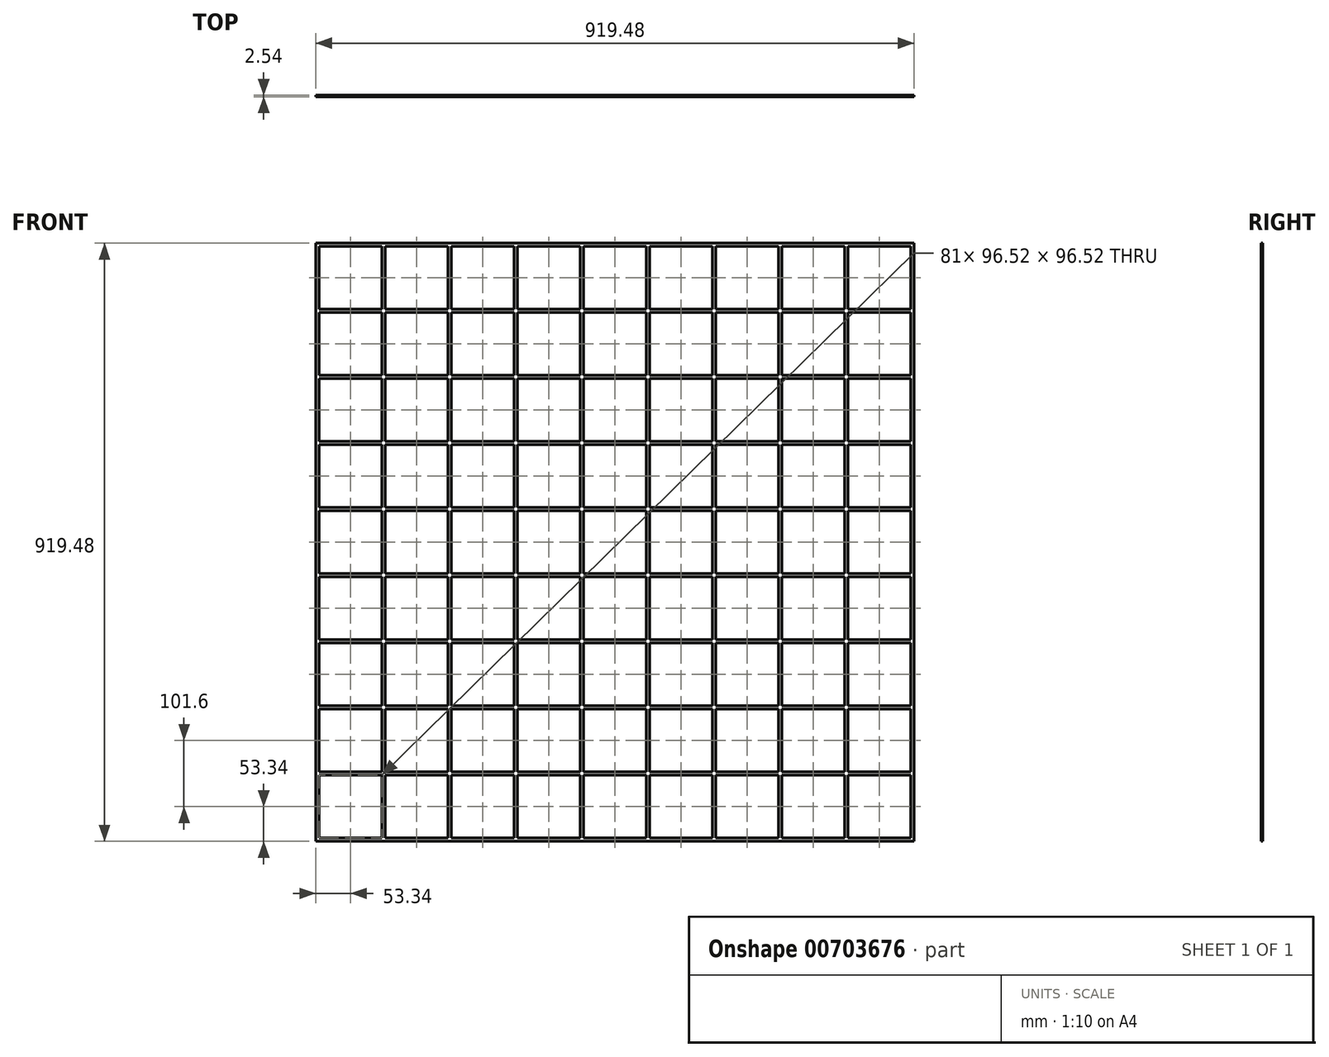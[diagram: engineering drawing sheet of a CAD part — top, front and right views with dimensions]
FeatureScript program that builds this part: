
annotation { "Feature Type Name" : "Feature", "Feature Type Description" : "" }
export const myFeature = defineFeature(function(context is Context, id is Id, definition is map)
    precondition{}
    {
        {
            var Q0;
            Q0=qCreatedBy(makeId("Front.planeOp"),FACE);
            var sketch = newSketch(context, id + "F0", { "sketchPlane" : qUnion([Q0])});
            skLineSegment(sketch, "E0.bottom", {"start": v(0, 0) * mm, "end": v(919.48, 0) * mm});
            skLineSegment(sketch, "E0.top", {"start": v(0, 919.48) * mm, "end": v(919.48, 919.48) * mm});
            skLineSegment(sketch, "E0.left", {"start": v(0, 0) * mm, "end": v(0, 919.48) * mm});
            skLineSegment(sketch, "E0.right", {"start": v(919.48, 0) * mm, "end": v(919.48, 919.48) * mm});
            skSolve(sketch);
        }
        {
            var Q0;
            Q0 = qSketchRegion(id + "F0", true);
            extrude(context, id + "F1", {"entities" : qUnion([Q0]), "depth" : 2.54 * mm, "offsetDistance" : 25.4 * mm});
        }
        {
            var Q0;
            Q0=makeQuery(id+"F0.imprint","IMPRINT",FACE,{"disambiguationData":[TD([[makeQuery(id+"F0.imprint","IMPRINT",EDGE,{"derivedFrom":sQuery(id+"F0.wireOp",EDGE,"E0.bottom")}),1.0]])]});
            var sketch = newSketch(context, id + "F2", { "sketchPlane" : qUnion([Q0])});
            skLineSegment(sketch, "E1.bottom", {"start": v(5.08, 914.4) * mm, "end": v(101.6, 914.4) * mm});
            skLineSegment(sketch, "E1.top", {"start": v(5.08, 817.88) * mm, "end": v(101.6, 817.88) * mm});
            skLineSegment(sketch, "E1.left", {"start": v(5.08, 914.4) * mm, "end": v(5.08, 817.88) * mm});
            skLineSegment(sketch, "E1.right", {"start": v(101.6, 914.4) * mm, "end": v(101.6, 817.88) * mm});
            skLineSegment(sketch, "E2.0.1.0", {"start": v(101.6, 812.8) * mm, "end": v(101.6, 716.28) * mm});
            skLineSegment(sketch, "E2.0.1.1", {"start": v(5.08, 812.8) * mm, "end": v(101.6, 812.8) * mm});
            skLineSegment(sketch, "E2.0.1.2", {"start": v(5.08, 812.8) * mm, "end": v(5.08, 716.28) * mm});
            skLineSegment(sketch, "E2.0.1.3", {"start": v(5.08, 716.28) * mm, "end": v(101.6, 716.28) * mm});
            skLineSegment(sketch, "E2.0.2.0", {"start": v(101.6, 711.2) * mm, "end": v(101.6, 614.68) * mm});
            skLineSegment(sketch, "E2.0.2.1", {"start": v(5.08, 711.2) * mm, "end": v(101.6, 711.2) * mm});
            skLineSegment(sketch, "E2.0.2.2", {"start": v(5.08, 711.2) * mm, "end": v(5.08, 614.68) * mm});
            skLineSegment(sketch, "E2.0.2.3", {"start": v(5.08, 614.68) * mm, "end": v(101.6, 614.68) * mm});
            skLineSegment(sketch, "E2.0.3.0", {"start": v(101.6, 609.6) * mm, "end": v(101.6, 513.08) * mm});
            skLineSegment(sketch, "E2.0.3.1", {"start": v(5.08, 609.6) * mm, "end": v(101.6, 609.6) * mm});
            skLineSegment(sketch, "E2.0.3.2", {"start": v(5.08, 609.6) * mm, "end": v(5.08, 513.08) * mm});
            skLineSegment(sketch, "E2.0.3.3", {"start": v(5.08, 513.08) * mm, "end": v(101.6, 513.08) * mm});
            skLineSegment(sketch, "E2.0.4.0", {"start": v(101.6, 508) * mm, "end": v(101.6, 411.48) * mm});
            skLineSegment(sketch, "E2.0.4.1", {"start": v(5.08, 508) * mm, "end": v(101.6, 508) * mm});
            skLineSegment(sketch, "E2.0.4.2", {"start": v(5.08, 508) * mm, "end": v(5.08, 411.48) * mm});
            skLineSegment(sketch, "E2.0.4.3", {"start": v(5.08, 411.48) * mm, "end": v(101.6, 411.48) * mm});
            skLineSegment(sketch, "E2.0.5.0", {"start": v(101.6, 406.4) * mm, "end": v(101.6, 309.88) * mm});
            skLineSegment(sketch, "E2.0.5.1", {"start": v(5.08, 406.4) * mm, "end": v(101.6, 406.4) * mm});
            skLineSegment(sketch, "E2.0.5.2", {"start": v(5.08, 406.4) * mm, "end": v(5.08, 309.88) * mm});
            skLineSegment(sketch, "E2.0.5.3", {"start": v(5.08, 309.88) * mm, "end": v(101.6, 309.88) * mm});
            skLineSegment(sketch, "E2.0.6.0", {"start": v(101.6, 304.8) * mm, "end": v(101.6, 208.28) * mm});
            skLineSegment(sketch, "E2.0.6.1", {"start": v(5.08, 304.8) * mm, "end": v(101.6, 304.8) * mm});
            skLineSegment(sketch, "E2.0.6.2", {"start": v(5.08, 304.8) * mm, "end": v(5.08, 208.28) * mm});
            skLineSegment(sketch, "E2.0.6.3", {"start": v(5.08, 208.28) * mm, "end": v(101.6, 208.28) * mm});
            skLineSegment(sketch, "E2.0.7.0", {"start": v(101.6, 203.2) * mm, "end": v(101.6, 106.68) * mm});
            skLineSegment(sketch, "E2.0.7.1", {"start": v(5.08, 203.2) * mm, "end": v(101.6, 203.2) * mm});
            skLineSegment(sketch, "E2.0.7.2", {"start": v(5.08, 203.2) * mm, "end": v(5.08, 106.68) * mm});
            skLineSegment(sketch, "E2.0.7.3", {"start": v(5.08, 106.68) * mm, "end": v(101.6, 106.68) * mm});
            skLineSegment(sketch, "E2.0.8.0", {"start": v(101.6, 101.6) * mm, "end": v(101.6, 5.08) * mm});
            skLineSegment(sketch, "E2.0.8.1", {"start": v(5.08, 101.6) * mm, "end": v(101.6, 101.6) * mm});
            skLineSegment(sketch, "E2.0.8.2", {"start": v(5.08, 101.6) * mm, "end": v(5.08, 5.08) * mm});
            skLineSegment(sketch, "E2.0.8.3", {"start": v(5.08, 5.08) * mm, "end": v(101.6, 5.08) * mm});
            skLineSegment(sketch, "E2.1.0.0", {"start": v(203.2, 914.4) * mm, "end": v(203.2, 817.88) * mm});
            skLineSegment(sketch, "E2.1.0.1", {"start": v(106.68, 914.4) * mm, "end": v(203.2, 914.4) * mm});
            skLineSegment(sketch, "E2.1.0.2", {"start": v(106.68, 914.4) * mm, "end": v(106.68, 817.88) * mm});
            skLineSegment(sketch, "E2.1.0.3", {"start": v(106.68, 817.88) * mm, "end": v(203.2, 817.88) * mm});
            skLineSegment(sketch, "E2.1.1.0", {"start": v(203.2, 812.8) * mm, "end": v(203.2, 716.28) * mm});
            skLineSegment(sketch, "E2.1.1.1", {"start": v(106.68, 812.8) * mm, "end": v(203.2, 812.8) * mm});
            skLineSegment(sketch, "E2.1.1.2", {"start": v(106.68, 812.8) * mm, "end": v(106.68, 716.28) * mm});
            skLineSegment(sketch, "E2.1.1.3", {"start": v(106.68, 716.28) * mm, "end": v(203.2, 716.28) * mm});
            skLineSegment(sketch, "E2.1.2.0", {"start": v(203.2, 711.2) * mm, "end": v(203.2, 614.68) * mm});
            skLineSegment(sketch, "E2.1.2.1", {"start": v(106.68, 711.2) * mm, "end": v(203.2, 711.2) * mm});
            skLineSegment(sketch, "E2.1.2.2", {"start": v(106.68, 711.2) * mm, "end": v(106.68, 614.68) * mm});
            skLineSegment(sketch, "E2.1.2.3", {"start": v(106.68, 614.68) * mm, "end": v(203.2, 614.68) * mm});
            skLineSegment(sketch, "E2.1.3.0", {"start": v(203.2, 609.6) * mm, "end": v(203.2, 513.08) * mm});
            skLineSegment(sketch, "E2.1.3.1", {"start": v(106.68, 609.6) * mm, "end": v(203.2, 609.6) * mm});
            skLineSegment(sketch, "E2.1.3.2", {"start": v(106.68, 609.6) * mm, "end": v(106.68, 513.08) * mm});
            skLineSegment(sketch, "E2.1.3.3", {"start": v(106.68, 513.08) * mm, "end": v(203.2, 513.08) * mm});
            skLineSegment(sketch, "E2.1.4.0", {"start": v(203.2, 508) * mm, "end": v(203.2, 411.48) * mm});
            skLineSegment(sketch, "E2.1.4.1", {"start": v(106.68, 508) * mm, "end": v(203.2, 508) * mm});
            skLineSegment(sketch, "E2.1.4.2", {"start": v(106.68, 508) * mm, "end": v(106.68, 411.48) * mm});
            skLineSegment(sketch, "E2.1.4.3", {"start": v(106.68, 411.48) * mm, "end": v(203.2, 411.48) * mm});
            skLineSegment(sketch, "E2.1.5.0", {"start": v(203.2, 406.4) * mm, "end": v(203.2, 309.88) * mm});
            skLineSegment(sketch, "E2.1.5.1", {"start": v(106.68, 406.4) * mm, "end": v(203.2, 406.4) * mm});
            skLineSegment(sketch, "E2.1.5.2", {"start": v(106.68, 406.4) * mm, "end": v(106.68, 309.88) * mm});
            skLineSegment(sketch, "E2.1.5.3", {"start": v(106.68, 309.88) * mm, "end": v(203.2, 309.88) * mm});
            skLineSegment(sketch, "E2.1.6.0", {"start": v(203.2, 304.8) * mm, "end": v(203.2, 208.28) * mm});
            skLineSegment(sketch, "E2.1.6.1", {"start": v(106.68, 304.8) * mm, "end": v(203.2, 304.8) * mm});
            skLineSegment(sketch, "E2.1.6.2", {"start": v(106.68, 304.8) * mm, "end": v(106.68, 208.28) * mm});
            skLineSegment(sketch, "E2.1.6.3", {"start": v(106.68, 208.28) * mm, "end": v(203.2, 208.28) * mm});
            skLineSegment(sketch, "E2.1.7.0", {"start": v(203.2, 203.2) * mm, "end": v(203.2, 106.68) * mm});
            skLineSegment(sketch, "E2.1.7.1", {"start": v(106.68, 203.2) * mm, "end": v(203.2, 203.2) * mm});
            skLineSegment(sketch, "E2.1.7.2", {"start": v(106.68, 203.2) * mm, "end": v(106.68, 106.68) * mm});
            skLineSegment(sketch, "E2.1.7.3", {"start": v(106.68, 106.68) * mm, "end": v(203.2, 106.68) * mm});
            skLineSegment(sketch, "E2.1.8.0", {"start": v(203.2, 101.6) * mm, "end": v(203.2, 5.08) * mm});
            skLineSegment(sketch, "E2.1.8.1", {"start": v(106.68, 101.6) * mm, "end": v(203.2, 101.6) * mm});
            skLineSegment(sketch, "E2.1.8.2", {"start": v(106.68, 101.6) * mm, "end": v(106.68, 5.08) * mm});
            skLineSegment(sketch, "E2.1.8.3", {"start": v(106.68, 5.08) * mm, "end": v(203.2, 5.08) * mm});
            skLineSegment(sketch, "E2.2.0.0", {"start": v(304.8, 914.4) * mm, "end": v(304.8, 817.88) * mm});
            skLineSegment(sketch, "E2.2.0.1", {"start": v(208.28, 914.4) * mm, "end": v(304.8, 914.4) * mm});
            skLineSegment(sketch, "E2.2.0.2", {"start": v(208.28, 914.4) * mm, "end": v(208.28, 817.88) * mm});
            skLineSegment(sketch, "E2.2.0.3", {"start": v(208.28, 817.88) * mm, "end": v(304.8, 817.88) * mm});
            skLineSegment(sketch, "E2.2.1.0", {"start": v(304.8, 812.8) * mm, "end": v(304.8, 716.28) * mm});
            skLineSegment(sketch, "E2.2.1.1", {"start": v(208.28, 812.8) * mm, "end": v(304.8, 812.8) * mm});
            skLineSegment(sketch, "E2.2.1.2", {"start": v(208.28, 812.8) * mm, "end": v(208.28, 716.28) * mm});
            skLineSegment(sketch, "E2.2.1.3", {"start": v(208.28, 716.28) * mm, "end": v(304.8, 716.28) * mm});
            skLineSegment(sketch, "E2.2.2.0", {"start": v(304.8, 711.2) * mm, "end": v(304.8, 614.68) * mm});
            skLineSegment(sketch, "E2.2.2.1", {"start": v(208.28, 711.2) * mm, "end": v(304.8, 711.2) * mm});
            skLineSegment(sketch, "E2.2.2.2", {"start": v(208.28, 711.2) * mm, "end": v(208.28, 614.68) * mm});
            skLineSegment(sketch, "E2.2.2.3", {"start": v(208.28, 614.68) * mm, "end": v(304.8, 614.68) * mm});
            skLineSegment(sketch, "E2.2.3.0", {"start": v(304.8, 609.6) * mm, "end": v(304.8, 513.08) * mm});
            skLineSegment(sketch, "E2.2.3.1", {"start": v(208.28, 609.6) * mm, "end": v(304.8, 609.6) * mm});
            skLineSegment(sketch, "E2.2.3.2", {"start": v(208.28, 609.6) * mm, "end": v(208.28, 513.08) * mm});
            skLineSegment(sketch, "E2.2.3.3", {"start": v(208.28, 513.08) * mm, "end": v(304.8, 513.08) * mm});
            skLineSegment(sketch, "E2.2.4.0", {"start": v(304.8, 508) * mm, "end": v(304.8, 411.48) * mm});
            skLineSegment(sketch, "E2.2.4.1", {"start": v(208.28, 508) * mm, "end": v(304.8, 508) * mm});
            skLineSegment(sketch, "E2.2.4.2", {"start": v(208.28, 508) * mm, "end": v(208.28, 411.48) * mm});
            skLineSegment(sketch, "E2.2.4.3", {"start": v(208.28, 411.48) * mm, "end": v(304.8, 411.48) * mm});
            skLineSegment(sketch, "E2.2.5.0", {"start": v(304.8, 406.4) * mm, "end": v(304.8, 309.88) * mm});
            skLineSegment(sketch, "E2.2.5.1", {"start": v(208.28, 406.4) * mm, "end": v(304.8, 406.4) * mm});
            skLineSegment(sketch, "E2.2.5.2", {"start": v(208.28, 406.4) * mm, "end": v(208.28, 309.88) * mm});
            skLineSegment(sketch, "E2.2.5.3", {"start": v(208.28, 309.88) * mm, "end": v(304.8, 309.88) * mm});
            skLineSegment(sketch, "E2.2.6.0", {"start": v(304.8, 304.8) * mm, "end": v(304.8, 208.28) * mm});
            skLineSegment(sketch, "E2.2.6.1", {"start": v(208.28, 304.8) * mm, "end": v(304.8, 304.8) * mm});
            skLineSegment(sketch, "E2.2.6.2", {"start": v(208.28, 304.8) * mm, "end": v(208.28, 208.28) * mm});
            skLineSegment(sketch, "E2.2.6.3", {"start": v(208.28, 208.28) * mm, "end": v(304.8, 208.28) * mm});
            skLineSegment(sketch, "E2.2.7.0", {"start": v(304.8, 203.2) * mm, "end": v(304.8, 106.68) * mm});
            skLineSegment(sketch, "E2.2.7.1", {"start": v(208.28, 203.2) * mm, "end": v(304.8, 203.2) * mm});
            skLineSegment(sketch, "E2.2.7.2", {"start": v(208.28, 203.2) * mm, "end": v(208.28, 106.68) * mm});
            skLineSegment(sketch, "E2.2.7.3", {"start": v(208.28, 106.68) * mm, "end": v(304.8, 106.68) * mm});
            skLineSegment(sketch, "E2.2.8.0", {"start": v(304.8, 101.6) * mm, "end": v(304.8, 5.08) * mm});
            skLineSegment(sketch, "E2.2.8.1", {"start": v(208.28, 101.6) * mm, "end": v(304.8, 101.6) * mm});
            skLineSegment(sketch, "E2.2.8.2", {"start": v(208.28, 101.6) * mm, "end": v(208.28, 5.08) * mm});
            skLineSegment(sketch, "E2.2.8.3", {"start": v(208.28, 5.08) * mm, "end": v(304.8, 5.08) * mm});
            skLineSegment(sketch, "E2.3.0.0", {"start": v(406.4, 914.4) * mm, "end": v(406.4, 817.88) * mm});
            skLineSegment(sketch, "E2.3.0.1", {"start": v(309.88, 914.4) * mm, "end": v(406.4, 914.4) * mm});
            skLineSegment(sketch, "E2.3.0.2", {"start": v(309.88, 914.4) * mm, "end": v(309.88, 817.88) * mm});
            skLineSegment(sketch, "E2.3.0.3", {"start": v(309.88, 817.88) * mm, "end": v(406.4, 817.88) * mm});
            skLineSegment(sketch, "E2.3.1.0", {"start": v(406.4, 812.8) * mm, "end": v(406.4, 716.28) * mm});
            skLineSegment(sketch, "E2.3.1.1", {"start": v(309.88, 812.8) * mm, "end": v(406.4, 812.8) * mm});
            skLineSegment(sketch, "E2.3.1.2", {"start": v(309.88, 812.8) * mm, "end": v(309.88, 716.28) * mm});
            skLineSegment(sketch, "E2.3.1.3", {"start": v(309.88, 716.28) * mm, "end": v(406.4, 716.28) * mm});
            skLineSegment(sketch, "E2.3.2.0", {"start": v(406.4, 711.2) * mm, "end": v(406.4, 614.68) * mm});
            skLineSegment(sketch, "E2.3.2.1", {"start": v(309.88, 711.2) * mm, "end": v(406.4, 711.2) * mm});
            skLineSegment(sketch, "E2.3.2.2", {"start": v(309.88, 711.2) * mm, "end": v(309.88, 614.68) * mm});
            skLineSegment(sketch, "E2.3.2.3", {"start": v(309.88, 614.68) * mm, "end": v(406.4, 614.68) * mm});
            skLineSegment(sketch, "E2.3.3.0", {"start": v(406.4, 609.6) * mm, "end": v(406.4, 513.08) * mm});
            skLineSegment(sketch, "E2.3.3.1", {"start": v(309.88, 609.6) * mm, "end": v(406.4, 609.6) * mm});
            skLineSegment(sketch, "E2.3.3.2", {"start": v(309.88, 609.6) * mm, "end": v(309.88, 513.08) * mm});
            skLineSegment(sketch, "E2.3.3.3", {"start": v(309.88, 513.08) * mm, "end": v(406.4, 513.08) * mm});
            skLineSegment(sketch, "E2.3.4.0", {"start": v(406.4, 508) * mm, "end": v(406.4, 411.48) * mm});
            skLineSegment(sketch, "E2.3.4.1", {"start": v(309.88, 508) * mm, "end": v(406.4, 508) * mm});
            skLineSegment(sketch, "E2.3.4.2", {"start": v(309.88, 508) * mm, "end": v(309.88, 411.48) * mm});
            skLineSegment(sketch, "E2.3.4.3", {"start": v(309.88, 411.48) * mm, "end": v(406.4, 411.48) * mm});
            skLineSegment(sketch, "E2.3.5.0", {"start": v(406.4, 406.4) * mm, "end": v(406.4, 309.88) * mm});
            skLineSegment(sketch, "E2.3.5.1", {"start": v(309.88, 406.4) * mm, "end": v(406.4, 406.4) * mm});
            skLineSegment(sketch, "E2.3.5.2", {"start": v(309.88, 406.4) * mm, "end": v(309.88, 309.88) * mm});
            skLineSegment(sketch, "E2.3.5.3", {"start": v(309.88, 309.88) * mm, "end": v(406.4, 309.88) * mm});
            skLineSegment(sketch, "E2.3.6.0", {"start": v(406.4, 304.8) * mm, "end": v(406.4, 208.28) * mm});
            skLineSegment(sketch, "E2.3.6.1", {"start": v(309.88, 304.8) * mm, "end": v(406.4, 304.8) * mm});
            skLineSegment(sketch, "E2.3.6.2", {"start": v(309.88, 304.8) * mm, "end": v(309.88, 208.28) * mm});
            skLineSegment(sketch, "E2.3.6.3", {"start": v(309.88, 208.28) * mm, "end": v(406.4, 208.28) * mm});
            skLineSegment(sketch, "E2.3.7.0", {"start": v(406.4, 203.2) * mm, "end": v(406.4, 106.68) * mm});
            skLineSegment(sketch, "E2.3.7.1", {"start": v(309.88, 203.2) * mm, "end": v(406.4, 203.2) * mm});
            skLineSegment(sketch, "E2.3.7.2", {"start": v(309.88, 203.2) * mm, "end": v(309.88, 106.68) * mm});
            skLineSegment(sketch, "E2.3.7.3", {"start": v(309.88, 106.68) * mm, "end": v(406.4, 106.68) * mm});
            skLineSegment(sketch, "E2.3.8.0", {"start": v(406.4, 101.6) * mm, "end": v(406.4, 5.08) * mm});
            skLineSegment(sketch, "E2.3.8.1", {"start": v(309.88, 101.6) * mm, "end": v(406.4, 101.6) * mm});
            skLineSegment(sketch, "E2.3.8.2", {"start": v(309.88, 101.6) * mm, "end": v(309.88, 5.08) * mm});
            skLineSegment(sketch, "E2.3.8.3", {"start": v(309.88, 5.08) * mm, "end": v(406.4, 5.08) * mm});
            skLineSegment(sketch, "E2.4.0.0", {"start": v(508, 914.4) * mm, "end": v(508, 817.88) * mm});
            skLineSegment(sketch, "E2.4.0.1", {"start": v(411.48, 914.4) * mm, "end": v(508, 914.4) * mm});
            skLineSegment(sketch, "E2.4.0.2", {"start": v(411.48, 914.4) * mm, "end": v(411.48, 817.88) * mm});
            skLineSegment(sketch, "E2.4.0.3", {"start": v(411.48, 817.88) * mm, "end": v(508, 817.88) * mm});
            skLineSegment(sketch, "E2.4.1.0", {"start": v(508, 812.8) * mm, "end": v(508, 716.28) * mm});
            skLineSegment(sketch, "E2.4.1.1", {"start": v(411.48, 812.8) * mm, "end": v(508, 812.8) * mm});
            skLineSegment(sketch, "E2.4.1.2", {"start": v(411.48, 812.8) * mm, "end": v(411.48, 716.28) * mm});
            skLineSegment(sketch, "E2.4.1.3", {"start": v(411.48, 716.28) * mm, "end": v(508, 716.28) * mm});
            skLineSegment(sketch, "E2.4.2.0", {"start": v(508, 711.2) * mm, "end": v(508, 614.68) * mm});
            skLineSegment(sketch, "E2.4.2.1", {"start": v(411.48, 711.2) * mm, "end": v(508, 711.2) * mm});
            skLineSegment(sketch, "E2.4.2.2", {"start": v(411.48, 711.2) * mm, "end": v(411.48, 614.68) * mm});
            skLineSegment(sketch, "E2.4.2.3", {"start": v(411.48, 614.68) * mm, "end": v(508, 614.68) * mm});
            skLineSegment(sketch, "E2.4.3.0", {"start": v(508, 609.6) * mm, "end": v(508, 513.08) * mm});
            skLineSegment(sketch, "E2.4.3.1", {"start": v(411.48, 609.6) * mm, "end": v(508, 609.6) * mm});
            skLineSegment(sketch, "E2.4.3.2", {"start": v(411.48, 609.6) * mm, "end": v(411.48, 513.08) * mm});
            skLineSegment(sketch, "E2.4.3.3", {"start": v(411.48, 513.08) * mm, "end": v(508, 513.08) * mm});
            skLineSegment(sketch, "E2.4.4.0", {"start": v(508, 508) * mm, "end": v(508, 411.48) * mm});
            skLineSegment(sketch, "E2.4.4.1", {"start": v(411.48, 508) * mm, "end": v(508, 508) * mm});
            skLineSegment(sketch, "E2.4.4.2", {"start": v(411.48, 508) * mm, "end": v(411.48, 411.48) * mm});
            skLineSegment(sketch, "E2.4.4.3", {"start": v(411.48, 411.48) * mm, "end": v(508, 411.48) * mm});
            skLineSegment(sketch, "E2.4.5.0", {"start": v(508, 406.4) * mm, "end": v(508, 309.88) * mm});
            skLineSegment(sketch, "E2.4.5.1", {"start": v(411.48, 406.4) * mm, "end": v(508, 406.4) * mm});
            skLineSegment(sketch, "E2.4.5.2", {"start": v(411.48, 406.4) * mm, "end": v(411.48, 309.88) * mm});
            skLineSegment(sketch, "E2.4.5.3", {"start": v(411.48, 309.88) * mm, "end": v(508, 309.88) * mm});
            skLineSegment(sketch, "E2.4.6.0", {"start": v(508, 304.8) * mm, "end": v(508, 208.28) * mm});
            skLineSegment(sketch, "E2.4.6.1", {"start": v(411.48, 304.8) * mm, "end": v(508, 304.8) * mm});
            skLineSegment(sketch, "E2.4.6.2", {"start": v(411.48, 304.8) * mm, "end": v(411.48, 208.28) * mm});
            skLineSegment(sketch, "E2.4.6.3", {"start": v(411.48, 208.28) * mm, "end": v(508, 208.28) * mm});
            skLineSegment(sketch, "E2.4.7.0", {"start": v(508, 203.2) * mm, "end": v(508, 106.68) * mm});
            skLineSegment(sketch, "E2.4.7.1", {"start": v(411.48, 203.2) * mm, "end": v(508, 203.2) * mm});
            skLineSegment(sketch, "E2.4.7.2", {"start": v(411.48, 203.2) * mm, "end": v(411.48, 106.68) * mm});
            skLineSegment(sketch, "E2.4.7.3", {"start": v(411.48, 106.68) * mm, "end": v(508, 106.68) * mm});
            skLineSegment(sketch, "E2.4.8.0", {"start": v(508, 101.6) * mm, "end": v(508, 5.08) * mm});
            skLineSegment(sketch, "E2.4.8.1", {"start": v(411.48, 101.6) * mm, "end": v(508, 101.6) * mm});
            skLineSegment(sketch, "E2.4.8.2", {"start": v(411.48, 101.6) * mm, "end": v(411.48, 5.08) * mm});
            skLineSegment(sketch, "E2.4.8.3", {"start": v(411.48, 5.08) * mm, "end": v(508, 5.08) * mm});
            skLineSegment(sketch, "E2.5.0.0", {"start": v(609.6, 914.4) * mm, "end": v(609.6, 817.88) * mm});
            skLineSegment(sketch, "E2.5.0.1", {"start": v(513.08, 914.4) * mm, "end": v(609.6, 914.4) * mm});
            skLineSegment(sketch, "E2.5.0.2", {"start": v(513.08, 914.4) * mm, "end": v(513.08, 817.88) * mm});
            skLineSegment(sketch, "E2.5.0.3", {"start": v(513.08, 817.88) * mm, "end": v(609.6, 817.88) * mm});
            skLineSegment(sketch, "E2.5.1.0", {"start": v(609.6, 812.8) * mm, "end": v(609.6, 716.28) * mm});
            skLineSegment(sketch, "E2.5.1.1", {"start": v(513.08, 812.8) * mm, "end": v(609.6, 812.8) * mm});
            skLineSegment(sketch, "E2.5.1.2", {"start": v(513.08, 812.8) * mm, "end": v(513.08, 716.28) * mm});
            skLineSegment(sketch, "E2.5.1.3", {"start": v(513.08, 716.28) * mm, "end": v(609.6, 716.28) * mm});
            skLineSegment(sketch, "E2.5.2.0", {"start": v(609.6, 711.2) * mm, "end": v(609.6, 614.68) * mm});
            skLineSegment(sketch, "E2.5.2.1", {"start": v(513.08, 711.2) * mm, "end": v(609.6, 711.2) * mm});
            skLineSegment(sketch, "E2.5.2.2", {"start": v(513.08, 711.2) * mm, "end": v(513.08, 614.68) * mm});
            skLineSegment(sketch, "E2.5.2.3", {"start": v(513.08, 614.68) * mm, "end": v(609.6, 614.68) * mm});
            skLineSegment(sketch, "E2.5.3.0", {"start": v(609.6, 609.6) * mm, "end": v(609.6, 513.08) * mm});
            skLineSegment(sketch, "E2.5.3.1", {"start": v(513.08, 609.6) * mm, "end": v(609.6, 609.6) * mm});
            skLineSegment(sketch, "E2.5.3.2", {"start": v(513.08, 609.6) * mm, "end": v(513.08, 513.08) * mm});
            skLineSegment(sketch, "E2.5.3.3", {"start": v(513.08, 513.08) * mm, "end": v(609.6, 513.08) * mm});
            skLineSegment(sketch, "E2.5.4.0", {"start": v(609.6, 508) * mm, "end": v(609.6, 411.48) * mm});
            skLineSegment(sketch, "E2.5.4.1", {"start": v(513.08, 508) * mm, "end": v(609.6, 508) * mm});
            skLineSegment(sketch, "E2.5.4.2", {"start": v(513.08, 508) * mm, "end": v(513.08, 411.48) * mm});
            skLineSegment(sketch, "E2.5.4.3", {"start": v(513.08, 411.48) * mm, "end": v(609.6, 411.48) * mm});
            skLineSegment(sketch, "E2.5.5.0", {"start": v(609.6, 406.4) * mm, "end": v(609.6, 309.88) * mm});
            skLineSegment(sketch, "E2.5.5.1", {"start": v(513.08, 406.4) * mm, "end": v(609.6, 406.4) * mm});
            skLineSegment(sketch, "E2.5.5.2", {"start": v(513.08, 406.4) * mm, "end": v(513.08, 309.88) * mm});
            skLineSegment(sketch, "E2.5.5.3", {"start": v(513.08, 309.88) * mm, "end": v(609.6, 309.88) * mm});
            skLineSegment(sketch, "E2.5.6.0", {"start": v(609.6, 304.8) * mm, "end": v(609.6, 208.28) * mm});
            skLineSegment(sketch, "E2.5.6.1", {"start": v(513.08, 304.8) * mm, "end": v(609.6, 304.8) * mm});
            skLineSegment(sketch, "E2.5.6.2", {"start": v(513.08, 304.8) * mm, "end": v(513.08, 208.28) * mm});
            skLineSegment(sketch, "E2.5.6.3", {"start": v(513.08, 208.28) * mm, "end": v(609.6, 208.28) * mm});
            skLineSegment(sketch, "E2.5.7.0", {"start": v(609.6, 203.2) * mm, "end": v(609.6, 106.68) * mm});
            skLineSegment(sketch, "E2.5.7.1", {"start": v(513.08, 203.2) * mm, "end": v(609.6, 203.2) * mm});
            skLineSegment(sketch, "E2.5.7.2", {"start": v(513.08, 203.2) * mm, "end": v(513.08, 106.68) * mm});
            skLineSegment(sketch, "E2.5.7.3", {"start": v(513.08, 106.68) * mm, "end": v(609.6, 106.68) * mm});
            skLineSegment(sketch, "E2.5.8.0", {"start": v(609.6, 101.6) * mm, "end": v(609.6, 5.08) * mm});
            skLineSegment(sketch, "E2.5.8.1", {"start": v(513.08, 101.6) * mm, "end": v(609.6, 101.6) * mm});
            skLineSegment(sketch, "E2.5.8.2", {"start": v(513.08, 101.6) * mm, "end": v(513.08, 5.08) * mm});
            skLineSegment(sketch, "E2.5.8.3", {"start": v(513.08, 5.08) * mm, "end": v(609.6, 5.08) * mm});
            skLineSegment(sketch, "E2.6.0.0", {"start": v(711.2, 914.4) * mm, "end": v(711.2, 817.88) * mm});
            skLineSegment(sketch, "E2.6.0.1", {"start": v(614.68, 914.4) * mm, "end": v(711.2, 914.4) * mm});
            skLineSegment(sketch, "E2.6.0.2", {"start": v(614.68, 914.4) * mm, "end": v(614.68, 817.88) * mm});
            skLineSegment(sketch, "E2.6.0.3", {"start": v(614.68, 817.88) * mm, "end": v(711.2, 817.88) * mm});
            skLineSegment(sketch, "E2.6.1.0", {"start": v(711.2, 812.8) * mm, "end": v(711.2, 716.28) * mm});
            skLineSegment(sketch, "E2.6.1.1", {"start": v(614.68, 812.8) * mm, "end": v(711.2, 812.8) * mm});
            skLineSegment(sketch, "E2.6.1.2", {"start": v(614.68, 812.8) * mm, "end": v(614.68, 716.28) * mm});
            skLineSegment(sketch, "E2.6.1.3", {"start": v(614.68, 716.28) * mm, "end": v(711.2, 716.28) * mm});
            skLineSegment(sketch, "E2.6.2.0", {"start": v(711.2, 711.2) * mm, "end": v(711.2, 614.68) * mm});
            skLineSegment(sketch, "E2.6.2.1", {"start": v(614.68, 711.2) * mm, "end": v(711.2, 711.2) * mm});
            skLineSegment(sketch, "E2.6.2.2", {"start": v(614.68, 711.2) * mm, "end": v(614.68, 614.68) * mm});
            skLineSegment(sketch, "E2.6.2.3", {"start": v(614.68, 614.68) * mm, "end": v(711.2, 614.68) * mm});
            skLineSegment(sketch, "E2.6.3.0", {"start": v(711.2, 609.6) * mm, "end": v(711.2, 513.08) * mm});
            skLineSegment(sketch, "E2.6.3.1", {"start": v(614.68, 609.6) * mm, "end": v(711.2, 609.6) * mm});
            skLineSegment(sketch, "E2.6.3.2", {"start": v(614.68, 609.6) * mm, "end": v(614.68, 513.08) * mm});
            skLineSegment(sketch, "E2.6.3.3", {"start": v(614.68, 513.08) * mm, "end": v(711.2, 513.08) * mm});
            skLineSegment(sketch, "E2.6.4.0", {"start": v(711.2, 508) * mm, "end": v(711.2, 411.48) * mm});
            skLineSegment(sketch, "E2.6.4.1", {"start": v(614.68, 508) * mm, "end": v(711.2, 508) * mm});
            skLineSegment(sketch, "E2.6.4.2", {"start": v(614.68, 508) * mm, "end": v(614.68, 411.48) * mm});
            skLineSegment(sketch, "E2.6.4.3", {"start": v(614.68, 411.48) * mm, "end": v(711.2, 411.48) * mm});
            skLineSegment(sketch, "E2.6.5.0", {"start": v(711.2, 406.4) * mm, "end": v(711.2, 309.88) * mm});
            skLineSegment(sketch, "E2.6.5.1", {"start": v(614.68, 406.4) * mm, "end": v(711.2, 406.4) * mm});
            skLineSegment(sketch, "E2.6.5.2", {"start": v(614.68, 406.4) * mm, "end": v(614.68, 309.88) * mm});
            skLineSegment(sketch, "E2.6.5.3", {"start": v(614.68, 309.88) * mm, "end": v(711.2, 309.88) * mm});
            skLineSegment(sketch, "E2.6.6.0", {"start": v(711.2, 304.8) * mm, "end": v(711.2, 208.28) * mm});
            skLineSegment(sketch, "E2.6.6.1", {"start": v(614.68, 304.8) * mm, "end": v(711.2, 304.8) * mm});
            skLineSegment(sketch, "E2.6.6.2", {"start": v(614.68, 304.8) * mm, "end": v(614.68, 208.28) * mm});
            skLineSegment(sketch, "E2.6.6.3", {"start": v(614.68, 208.28) * mm, "end": v(711.2, 208.28) * mm});
            skLineSegment(sketch, "E2.6.7.0", {"start": v(711.2, 203.2) * mm, "end": v(711.2, 106.68) * mm});
            skLineSegment(sketch, "E2.6.7.1", {"start": v(614.68, 203.2) * mm, "end": v(711.2, 203.2) * mm});
            skLineSegment(sketch, "E2.6.7.2", {"start": v(614.68, 203.2) * mm, "end": v(614.68, 106.68) * mm});
            skLineSegment(sketch, "E2.6.7.3", {"start": v(614.68, 106.68) * mm, "end": v(711.2, 106.68) * mm});
            skLineSegment(sketch, "E2.6.8.0", {"start": v(711.2, 101.6) * mm, "end": v(711.2, 5.08) * mm});
            skLineSegment(sketch, "E2.6.8.1", {"start": v(614.68, 101.6) * mm, "end": v(711.2, 101.6) * mm});
            skLineSegment(sketch, "E2.6.8.2", {"start": v(614.68, 101.6) * mm, "end": v(614.68, 5.08) * mm});
            skLineSegment(sketch, "E2.6.8.3", {"start": v(614.68, 5.08) * mm, "end": v(711.2, 5.08) * mm});
            skLineSegment(sketch, "E2.7.0.0", {"start": v(812.8, 914.4) * mm, "end": v(812.8, 817.88) * mm});
            skLineSegment(sketch, "E2.7.0.1", {"start": v(716.28, 914.4) * mm, "end": v(812.8, 914.4) * mm});
            skLineSegment(sketch, "E2.7.0.2", {"start": v(716.28, 914.4) * mm, "end": v(716.28, 817.88) * mm});
            skLineSegment(sketch, "E2.7.0.3", {"start": v(716.28, 817.88) * mm, "end": v(812.8, 817.88) * mm});
            skLineSegment(sketch, "E2.7.1.0", {"start": v(812.8, 812.8) * mm, "end": v(812.8, 716.28) * mm});
            skLineSegment(sketch, "E2.7.1.1", {"start": v(716.28, 812.8) * mm, "end": v(812.8, 812.8) * mm});
            skLineSegment(sketch, "E2.7.1.2", {"start": v(716.28, 812.8) * mm, "end": v(716.28, 716.28) * mm});
            skLineSegment(sketch, "E2.7.1.3", {"start": v(716.28, 716.28) * mm, "end": v(812.8, 716.28) * mm});
            skLineSegment(sketch, "E2.7.2.0", {"start": v(812.8, 711.2) * mm, "end": v(812.8, 614.68) * mm});
            skLineSegment(sketch, "E2.7.2.1", {"start": v(716.28, 711.2) * mm, "end": v(812.8, 711.2) * mm});
            skLineSegment(sketch, "E2.7.2.2", {"start": v(716.28, 711.2) * mm, "end": v(716.28, 614.68) * mm});
            skLineSegment(sketch, "E2.7.2.3", {"start": v(716.28, 614.68) * mm, "end": v(812.8, 614.68) * mm});
            skLineSegment(sketch, "E2.7.3.0", {"start": v(812.8, 609.6) * mm, "end": v(812.8, 513.08) * mm});
            skLineSegment(sketch, "E2.7.3.1", {"start": v(716.28, 609.6) * mm, "end": v(812.8, 609.6) * mm});
            skLineSegment(sketch, "E2.7.3.2", {"start": v(716.28, 609.6) * mm, "end": v(716.28, 513.08) * mm});
            skLineSegment(sketch, "E2.7.3.3", {"start": v(716.28, 513.08) * mm, "end": v(812.8, 513.08) * mm});
            skLineSegment(sketch, "E2.7.4.0", {"start": v(812.8, 508) * mm, "end": v(812.8, 411.48) * mm});
            skLineSegment(sketch, "E2.7.4.1", {"start": v(716.28, 508) * mm, "end": v(812.8, 508) * mm});
            skLineSegment(sketch, "E2.7.4.2", {"start": v(716.28, 508) * mm, "end": v(716.28, 411.48) * mm});
            skLineSegment(sketch, "E2.7.4.3", {"start": v(716.28, 411.48) * mm, "end": v(812.8, 411.48) * mm});
            skLineSegment(sketch, "E2.7.5.0", {"start": v(812.8, 406.4) * mm, "end": v(812.8, 309.88) * mm});
            skLineSegment(sketch, "E2.7.5.1", {"start": v(716.28, 406.4) * mm, "end": v(812.8, 406.4) * mm});
            skLineSegment(sketch, "E2.7.5.2", {"start": v(716.28, 406.4) * mm, "end": v(716.28, 309.88) * mm});
            skLineSegment(sketch, "E2.7.5.3", {"start": v(716.28, 309.88) * mm, "end": v(812.8, 309.88) * mm});
            skLineSegment(sketch, "E2.7.6.0", {"start": v(812.8, 304.8) * mm, "end": v(812.8, 208.28) * mm});
            skLineSegment(sketch, "E2.7.6.1", {"start": v(716.28, 304.8) * mm, "end": v(812.8, 304.8) * mm});
            skLineSegment(sketch, "E2.7.6.2", {"start": v(716.28, 304.8) * mm, "end": v(716.28, 208.28) * mm});
            skLineSegment(sketch, "E2.7.6.3", {"start": v(716.28, 208.28) * mm, "end": v(812.8, 208.28) * mm});
            skLineSegment(sketch, "E2.7.7.0", {"start": v(812.8, 203.2) * mm, "end": v(812.8, 106.68) * mm});
            skLineSegment(sketch, "E2.7.7.1", {"start": v(716.28, 203.2) * mm, "end": v(812.8, 203.2) * mm});
            skLineSegment(sketch, "E2.7.7.2", {"start": v(716.28, 203.2) * mm, "end": v(716.28, 106.68) * mm});
            skLineSegment(sketch, "E2.7.7.3", {"start": v(716.28, 106.68) * mm, "end": v(812.8, 106.68) * mm});
            skLineSegment(sketch, "E2.7.8.0", {"start": v(812.8, 101.6) * mm, "end": v(812.8, 5.08) * mm});
            skLineSegment(sketch, "E2.7.8.1", {"start": v(716.28, 101.6) * mm, "end": v(812.8, 101.6) * mm});
            skLineSegment(sketch, "E2.7.8.2", {"start": v(716.28, 101.6) * mm, "end": v(716.28, 5.08) * mm});
            skLineSegment(sketch, "E2.7.8.3", {"start": v(716.28, 5.08) * mm, "end": v(812.8, 5.08) * mm});
            skLineSegment(sketch, "E2.8.0.0", {"start": v(914.4, 914.4) * mm, "end": v(914.4, 817.88) * mm});
            skLineSegment(sketch, "E2.8.0.1", {"start": v(817.88, 914.4) * mm, "end": v(914.4, 914.4) * mm});
            skLineSegment(sketch, "E2.8.0.2", {"start": v(817.88, 914.4) * mm, "end": v(817.88, 817.88) * mm});
            skLineSegment(sketch, "E2.8.0.3", {"start": v(817.88, 817.88) * mm, "end": v(914.4, 817.88) * mm});
            skLineSegment(sketch, "E2.8.1.0", {"start": v(914.4, 812.8) * mm, "end": v(914.4, 716.28) * mm});
            skLineSegment(sketch, "E2.8.1.1", {"start": v(817.88, 812.8) * mm, "end": v(914.4, 812.8) * mm});
            skLineSegment(sketch, "E2.8.1.2", {"start": v(817.88, 812.8) * mm, "end": v(817.88, 716.28) * mm});
            skLineSegment(sketch, "E2.8.1.3", {"start": v(817.88, 716.28) * mm, "end": v(914.4, 716.28) * mm});
            skLineSegment(sketch, "E2.8.2.0", {"start": v(914.4, 711.2) * mm, "end": v(914.4, 614.68) * mm});
            skLineSegment(sketch, "E2.8.2.1", {"start": v(817.88, 711.2) * mm, "end": v(914.4, 711.2) * mm});
            skLineSegment(sketch, "E2.8.2.2", {"start": v(817.88, 711.2) * mm, "end": v(817.88, 614.68) * mm});
            skLineSegment(sketch, "E2.8.2.3", {"start": v(817.88, 614.68) * mm, "end": v(914.4, 614.68) * mm});
            skLineSegment(sketch, "E2.8.3.0", {"start": v(914.4, 609.6) * mm, "end": v(914.4, 513.08) * mm});
            skLineSegment(sketch, "E2.8.3.1", {"start": v(817.88, 609.6) * mm, "end": v(914.4, 609.6) * mm});
            skLineSegment(sketch, "E2.8.3.2", {"start": v(817.88, 609.6) * mm, "end": v(817.88, 513.08) * mm});
            skLineSegment(sketch, "E2.8.3.3", {"start": v(817.88, 513.08) * mm, "end": v(914.4, 513.08) * mm});
            skLineSegment(sketch, "E2.8.4.0", {"start": v(914.4, 508) * mm, "end": v(914.4, 411.48) * mm});
            skLineSegment(sketch, "E2.8.4.1", {"start": v(817.88, 508) * mm, "end": v(914.4, 508) * mm});
            skLineSegment(sketch, "E2.8.4.2", {"start": v(817.88, 508) * mm, "end": v(817.88, 411.48) * mm});
            skLineSegment(sketch, "E2.8.4.3", {"start": v(817.88, 411.48) * mm, "end": v(914.4, 411.48) * mm});
            skLineSegment(sketch, "E2.8.5.0", {"start": v(914.4, 406.4) * mm, "end": v(914.4, 309.88) * mm});
            skLineSegment(sketch, "E2.8.5.1", {"start": v(817.88, 406.4) * mm, "end": v(914.4, 406.4) * mm});
            skLineSegment(sketch, "E2.8.5.2", {"start": v(817.88, 406.4) * mm, "end": v(817.88, 309.88) * mm});
            skLineSegment(sketch, "E2.8.5.3", {"start": v(817.88, 309.88) * mm, "end": v(914.4, 309.88) * mm});
            skLineSegment(sketch, "E2.8.6.0", {"start": v(914.4, 304.8) * mm, "end": v(914.4, 208.28) * mm});
            skLineSegment(sketch, "E2.8.6.1", {"start": v(817.88, 304.8) * mm, "end": v(914.4, 304.8) * mm});
            skLineSegment(sketch, "E2.8.6.2", {"start": v(817.88, 304.8) * mm, "end": v(817.88, 208.28) * mm});
            skLineSegment(sketch, "E2.8.6.3", {"start": v(817.88, 208.28) * mm, "end": v(914.4, 208.28) * mm});
            skLineSegment(sketch, "E2.8.7.0", {"start": v(914.4, 203.2) * mm, "end": v(914.4, 106.68) * mm});
            skLineSegment(sketch, "E2.8.7.1", {"start": v(817.88, 203.2) * mm, "end": v(914.4, 203.2) * mm});
            skLineSegment(sketch, "E2.8.7.2", {"start": v(817.88, 203.2) * mm, "end": v(817.88, 106.68) * mm});
            skLineSegment(sketch, "E2.8.7.3", {"start": v(817.88, 106.68) * mm, "end": v(914.4, 106.68) * mm});
            skLineSegment(sketch, "E2.8.8.0", {"start": v(914.4, 101.6) * mm, "end": v(914.4, 5.08) * mm});
            skLineSegment(sketch, "E2.8.8.1", {"start": v(817.88, 101.6) * mm, "end": v(914.4, 101.6) * mm});
            skLineSegment(sketch, "E2.8.8.2", {"start": v(817.88, 101.6) * mm, "end": v(817.88, 5.08) * mm});
            skLineSegment(sketch, "E2.8.8.3", {"start": v(817.88, 5.08) * mm, "end": v(914.4, 5.08) * mm});
            skLineSegment(sketch, "E2.direction1", {"start": v(101.6, 817.88) * mm, "end": v(203.2, 817.88) * mm, "construction": true});
            skLineSegment(sketch, "E2.direction2", {"start": v(101.6, 817.88) * mm, "end": v(101.6, 716.28) * mm, "construction": true});
            skSolve(sketch);
        }
        {
            var Q0;
            Q0 = qSketchRegion(id + "F2", true);
            extrude(context, id + "F3", {"entities" : qUnion([Q0]), "operationType" : NewBodyOperationType.REMOVE, "depth" : 2.54 * mm, "offsetDistance" : 25.4 * mm});
        }
    });
